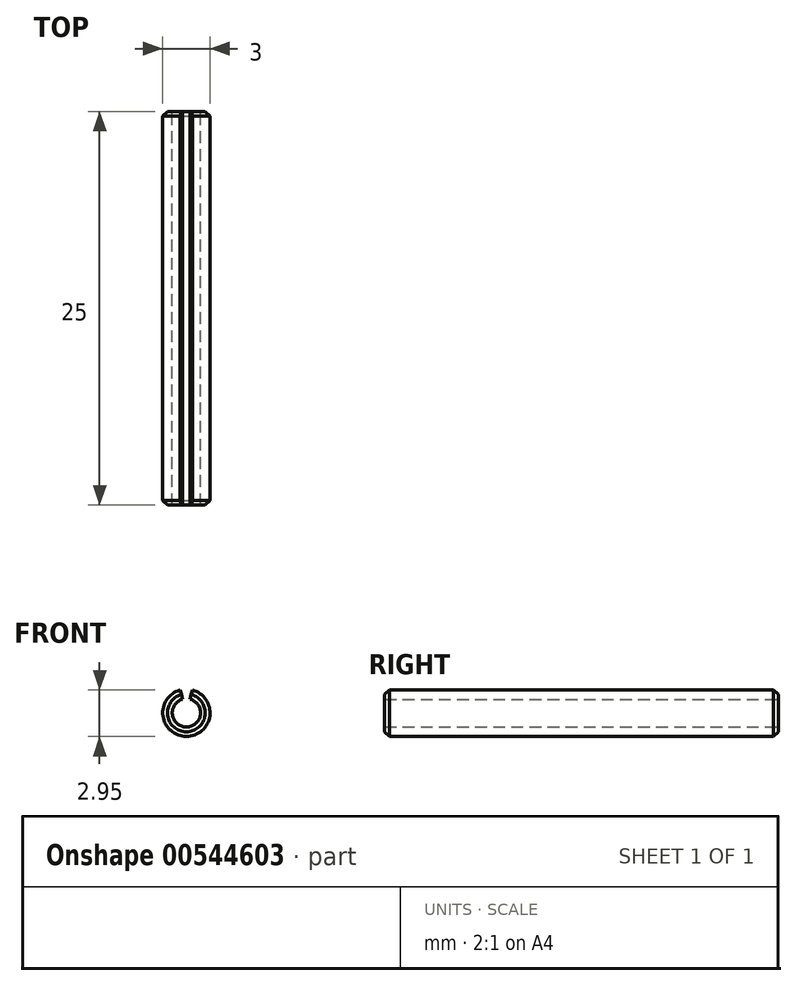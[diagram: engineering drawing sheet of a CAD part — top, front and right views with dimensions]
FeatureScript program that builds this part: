
annotation { "Feature Type Name" : "Feature", "Feature Type Description" : "" }
export const myFeature = defineFeature(function(context is Context, id is Id, definition is map)
    precondition{}
    {
        {
            var Q0;
            Q0=qCreatedBy(makeId("Front.planeOp"),FACE);
            var sketch = newSketch(context, id + "F0", { "sketchPlane" : qUnion([Q0])});
            skCircle(sketch, "E0", {"center": v(0, 0) * mm, "radius": 1.5 * mm});
            skSolve(sketch);
        }
        {
            var Q0;
            Q0=qSketchRegion(id+"F0",true);
            extrude(context, id + "F1", {"entities" : qUnion([Q0]), "depth" : 25 * mm, "offsetDistance" : 25 * mm});
        }
        {
            var Q0;
            Q0=makeQuery(id+"F1.opExtrude","CAP_FACE",FACE,{"disambiguationData":[OSD([sQuery(id+"F0.wireOp",EDGE,"E0")])],"isStart":false});
            var Q1;
            Q1=makeQuery(id+"F1.opExtrude","CAP_FACE",FACE,{"disambiguationData":[OSD([sQuery(id+"F0.wireOp",EDGE,"E0")])],"isStart":true});
            shell(context, id + "F2", {"entities" : qUnion([Q0, Q1]), "thickness" : 0.6 * mm});
        }
        {
            var Q0;
            Q0=makeQuery(id+"F1.opExtrude","CAP_EDGE",EDGE,{"disambiguationData":[OSD([sQuery(id+"F0.wireOp",EDGE,"E0")])],"isStart":false});
            chamfer(context, id + "F3", {"entities" : qUnion([Q0]), "width" : 0.3 * mm, "tangentPropagation" : true});
        }
        {
            var Q0;
            Q0=makeQuery(id+"F1.opExtrude","CAP_EDGE",EDGE,{"disambiguationData":[OSD([sQuery(id+"F0.wireOp",EDGE,"E0")])],"isStart":true});
            chamfer(context, id + "F4", {"entities" : qUnion([Q0]), "width" : .3 * mm, "tangentPropagation" : true});
        }
        {
            var Q0;
            Q0=makeQuery(id+"F1.opExtrude","CAP_FACE",FACE,{"disambiguationData":[OSD([sQuery(id+"F0.wireOp",EDGE,"E0")])],"isStart":false});
            var sketch = newSketch(context, id + "F5", { "sketchPlane" : qUnion([Q0])});
            skLineSegment(sketch, "E1", {"start": v(0, 0) * mm, "end": v(0.49, 1.83) * mm});
            skLineSegment(sketch, "E2", {"start": v(0, 0) * mm, "end": v(0, 3) * mm, "construction": true});
            skLineSegment(sketch, "E3.MirrorCS", {"start": v(0, 0) * mm, "end": v(-0.49, 1.83) * mm});
            skLineSegment(sketch, "E4", {"start": v(-0.49, 1.83) * mm, "end": v(0.49, 1.83) * mm});
            skSolve(sketch);
        }
        {
            var Q0;
            Q0=qSketchRegion(id+"F5",true);
            extrude(context, id + "F6", {"entities" : qUnion([Q0]), "operationType" : NewBodyOperationType.REMOVE, "endBound" : BoundingType.THROUGH_ALL, "oppositeDirection" : true, "depth" : 25 * mm, "offsetDistance" : 25 * mm});
        }
    });
